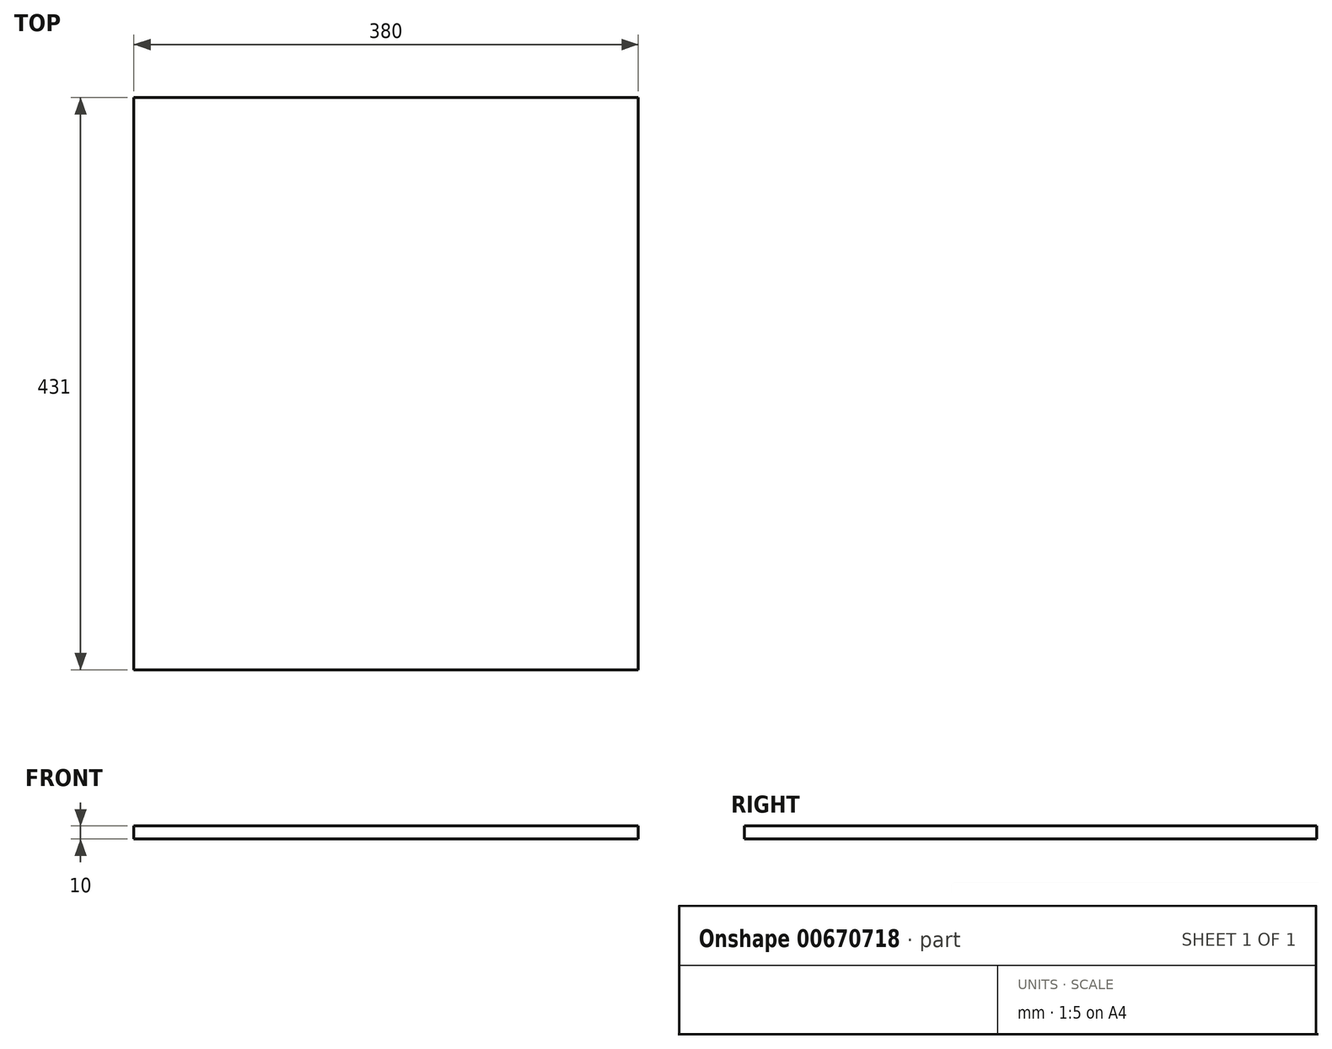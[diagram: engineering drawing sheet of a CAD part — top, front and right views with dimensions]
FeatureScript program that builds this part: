
annotation { "Feature Type Name" : "Feature", "Feature Type Description" : "" }
export const myFeature = defineFeature(function(context is Context, id is Id, definition is map)
    precondition{}
    {
        {
            var Q0;
            Q0=qCreatedBy(makeId("Top.planeOp"),FACE);
            var sketch = newSketch(context, id + "F0", { "sketchPlane" : qUnion([Q0])});
            skLineSegment(sketch, "E0.bottom", {"start": v(190, 215.5) * mm, "end": v(-190, 215.5) * mm});
            skLineSegment(sketch, "E0.top", {"start": v(190, -215.5) * mm, "end": v(-190, -215.5) * mm});
            skLineSegment(sketch, "E0.left", {"start": v(190, 215.5) * mm, "end": v(190, -215.5) * mm});
            skLineSegment(sketch, "E0.right", {"start": v(-190, 215.5) * mm, "end": v(-190, -215.5) * mm});
            skPoint(sketch, "E0.middle", {"position": v(0, 0) * mm});
            skSolve(sketch);
        }
        {
            var Q0;
            Q0 = qSketchRegion(id + "F0", true);
            extrude(context, id + "F1", {"entities" : qUnion([Q0]), "endBound" : BoundingType.SYMMETRIC, "depth" : 10 * mm, "offsetDistance" : 25 * mm});
        }
    });
